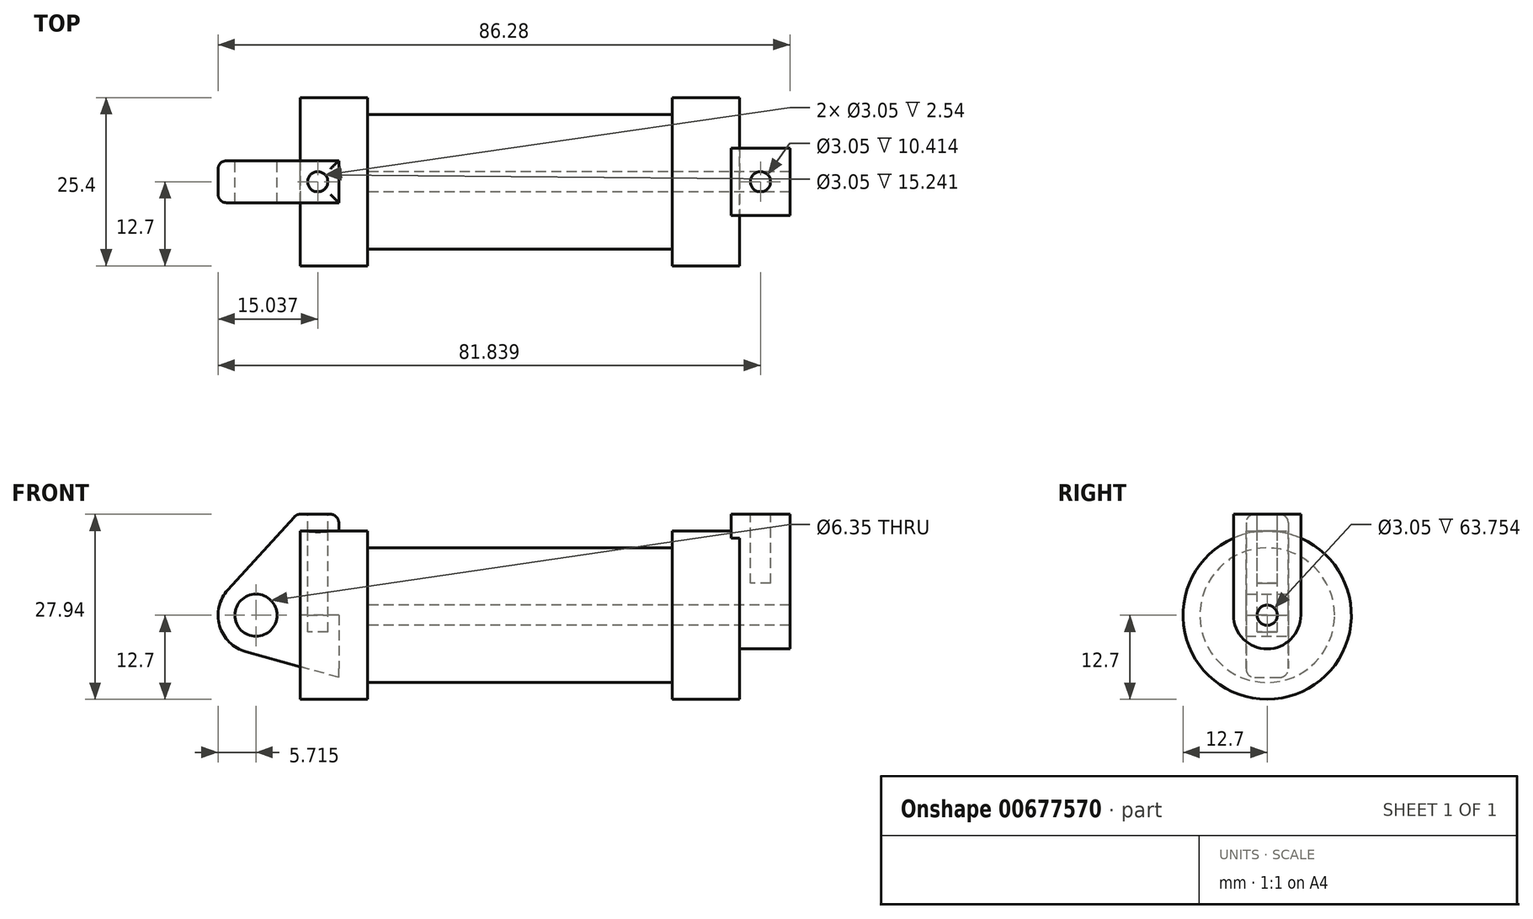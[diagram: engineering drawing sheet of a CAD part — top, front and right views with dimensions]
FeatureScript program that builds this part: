
annotation { "Feature Type Name" : "Feature", "Feature Type Description" : "" }
export const myFeature = defineFeature(function(context is Context, id is Id, definition is map)
    precondition{}
    {
        {
            var Q0;
            Q0=qCreatedBy(makeId("Front.planeOp"),FACE);
            var sketch = newSketch(context, id + "F0", { "sketchPlane" : qUnion([Q0])});
            skLineSegment(sketch, "E0", {"start": v(0, 0) * mm, "end": v(0, 12.7) * mm});
            skLineSegment(sketch, "E1", {"start": v(0, 12.7) * mm, "end": v(10.16, 12.7) * mm});
            skLineSegment(sketch, "E2", {"start": v(10.16, 12.7) * mm, "end": v(10.16, 10.16) * mm});
            skLineSegment(sketch, "E3", {"start": v(10.16, 10.16) * mm, "end": v(56.13, 10.16) * mm});
            skLineSegment(sketch, "E4", {"start": v(56.13, 10.16) * mm, "end": v(56.13, 12.7) * mm});
            skLineSegment(sketch, "E5", {"start": v(56.13, 12.7) * mm, "end": v(66.3, 12.7) * mm});
            skLineSegment(sketch, "E6", {"start": v(66.3, 12.7) * mm, "end": v(66.3, 0) * mm});
            skLineSegment(sketch, "E7", {"start": v(66.3, 0) * mm, "end": v(0, 0) * mm});
            skLineSegment(sketch, "E8", {"start": v(5.84, 15.24) * mm, "end": v(-0.5, 15.24) * mm});
            skLineSegment(sketch, "E9", {"start": v(-0.5, 15.24) * mm, "end": v(-10.88, 3.85) * mm});
            skLineSegment(sketch, "E10", {"start": v(0, 0) * mm, "end": v(-6.65, 0) * mm});
            skCircle(sketch, "E11", {"center": v(-6.65, 0) * mm, "radius": 5.72 * mm});
            skCircle(sketch, "E12", {"center": v(-6.65, 0) * mm, "radius": 3.18 * mm});
            skLineSegment(sketch, "E13", {"start": v(5.84, 15.24) * mm, "end": v(5.84, -9.4) * mm});
            skLineSegment(sketch, "E14", {"start": v(5.84, -9.4) * mm, "end": v(-8.18, -5.5) * mm});
            skSolve(sketch);
        }
        {
            var Q0;
            {var subQ0=sQuery(id+"F0.wireOp",EDGE,"E2");Q0=makeQuery(id+"F0.imprint","IMPRINT",FACE,{"disambiguationData":[TD([[makeQuery(id+"F0.imprint","IMPRINT",EDGE,{"derivedFrom":subQ0}),-1.0]])]});}
            var Q1;
            {var subQ0=sQuery(id+"F0.wireOp",EDGE,"E0");Q1=makeQuery(id+"F0.imprint","IMPRINT",FACE,{"disambiguationData":[TD([[makeQuery(id+"F0.imprint","IMPRINT",EDGE,{"derivedFrom":subQ0}),-1.0]])]});}
            var Q2;
            Q2=sQuery(id+"F0.wireOp",EDGE,"E7");
            revolve(context, id + "F1", {"entities" : qUnion([Q0, Q1]), "axis" : qUnion([Q2]), "revolveType" : RevolveType.FULL});
        }
        {
            var Q0;
            {var subQ0=sQuery(id+"F0.wireOp",EDGE,"E14");Q0=makeQuery(id+"F0.imprint","IMPRINT",FACE,{"disambiguationData":[TD([[makeQuery(id+"F0.imprint","IMPRINT",EDGE,{"derivedFrom":subQ0}),-1.0]])]});}
            var Q1;
            {var subQ1=sQuery(id+"F0.wireOp",EDGE,"E0");Q1=makeQuery(id+"F0.imprint","IMPRINT",FACE,{"disambiguationData":[TD([[makeQuery(id+"F0.imprint","IMPRINT",EDGE,{"derivedFrom":subQ1}),1.0]])]});}
            var Q2;
            {var subQ5=sQuery(id+"F0.wireOp",EDGE,"E12");Q2=makeQuery(id+"F0.imprint","IMPRINT",FACE,{"disambiguationData":[TD([[makeQuery(id+"F0.imprint","IMPRINT",EDGE,{"derivedFrom":subQ5}),-1.0]])]});}
            extrude(context, id + "F2", {"entities" : qUnion([Q0, Q1, Q2]), "endBound" : BoundingType.SYMMETRIC, "depth" : 6.35 * mm, "offsetDistance" : 25.4 * mm});
        }
        {
            var Q0;
            Q0=makeQuery(id+"F1.opRevolve","SWEPT_FACE",FACE,{"disambiguationData":[OSD([sQuery(id+"F0.wireOp",EDGE,"E6")])]});
            var sketch = newSketch(context, id + "F3", { "sketchPlane" : qUnion([Q0])});
            skCircle(sketch, "E15", {"center": v(0, 0) * mm, "radius": 1.52 * mm});
            skCircle(sketch, "E16", {"center": v(0, 0) * mm, "radius": 5.08 * mm});
            skLineSegment(sketch, "E17", {"start": v(5.08, 0) * mm, "end": v(5.08, 15.24) * mm});
            skLineSegment(sketch, "E18", {"start": v(-5.08, 0) * mm, "end": v(-5.08, 15.24) * mm});
            skLineSegment(sketch, "E19", {"start": v(-5.08, 15.24) * mm, "end": v(5.08, 15.24) * mm});
            skSolve(sketch);
        }
        {
            var Q0;
            Q0=makeQuery(id+"F3.imprint","IMPRINT",FACE,{"disambiguationData":[TD([[makeQuery(id+"F3.imprint","IMPRINT",EDGE,{"derivedFrom":sQuery(id+"F3.wireOp",EDGE,"E15")}),-1.0]])]});
            var Q1;
            {var subQ0=sQuery(id+"F3.wireOp",EDGE,"E19");Q1=makeQuery(id+"F3.imprint","IMPRINT",FACE,{"disambiguationData":[TD([[makeQuery(id+"F3.imprint","IMPRINT",EDGE,{"derivedFrom":subQ0}),-1.0]])]});}
            var Q2;
            {var subQ0=sQuery(id+"F3.wireOp",EDGE,"E17");var subQ1=sQuery(id+"F3.wireOp",EDGE,"E16");var subQ2=makeQuery(id+"F3.imprint","INTERSECT",VERTEX,{"derivedFrom":[subQ1,subQ0]});Q2=makeQuery(id+"F3.imprint","IMPRINT",FACE,{"disambiguationData":[TD([[makeQuery(id+"F3.imprint","IMPRINT",EDGE,{"disambiguationData":[TD([[subQ2,-1.0]])],"derivedFrom":subQ1}),-1.0]])]});}
            extrude(context, id + "F4", {"entities" : qUnion([Q0, Q1, Q2]), "operationType" : NewBodyOperationType.ADD, "depth" : 7.62 * mm, "offsetDistance" : 25.4 * mm, "hasSecondDirection" : true, "secondDirectionOppositeDirection" : true, "secondDirectionDepth" : 1.27 * mm});
        }
        {
            var Q0;
            Q0=makeQuery(id+"F4.boolean.opBoolean","SPLIT",FACE,{"disambiguationData":[TD([makeQuery(id+"F4.opExtrude","SWEPT_FACE",FACE,{"disambiguationData":[OSD([sQuery(id+"F3.wireOp",EDGE,"E15")])]})])],"derivedFrom":makeQuery(id+"F1.opRevolve","SWEPT_FACE",FACE,{"disambiguationData":[OSD([sQuery(id+"F0.wireOp",EDGE,"E6")])]})});
            var Q1;
            Q1=makeQuery(id+"F1.opRevolve","SWEPT_FACE",FACE,{"disambiguationData":[OSD([sQuery(id+"F0.wireOp",EDGE,"E2")])]});
            var Q2;
            Q2=makeQuery(id+"F1.opRevolve","SWEPT_BODY",BODY,{"disambiguationData":[OSD([sQuery(id+"F0.wireOp",EDGE,"E0"),sQuery(id+"F0.wireOp",EDGE,"E1"),sQuery(id+"F0.wireOp",EDGE,"E2"),sQuery(id+"F0.wireOp",EDGE,"E3"),sQuery(id+"F0.wireOp",EDGE,"E4"),sQuery(id+"F0.wireOp",EDGE,"E5"),sQuery(id+"F0.wireOp",EDGE,"E6"),sQuery(id+"F0.wireOp",EDGE,"E7")])]});
            extrude(context, id + "F5", {"entities" : qUnion([Q0]), "operationType" : NewBodyOperationType.REMOVE, "endBound" : BoundingType.UP_TO_SURFACE, "oppositeDirection" : true, "depth" : 25.4 * mm, "endBoundEntityFace" : qUnion([Q1]), "endBoundEntityBody" : qUnion([Q2]), "offsetDistance" : 25.4 * mm});
        }
        {
            var Q0;
            Q0=makeQuery(id+"F2.opExtrude","SWEPT_FACE",FACE,{"disambiguationData":[OSD([sQuery(id+"F0.wireOp",EDGE,"E8")])]});
            var sketch = newSketch(context, id + "F6", { "sketchPlane" : qUnion([Q0])});
            skCircle(sketch, "E20", {"center": v(2.67, 0) * mm, "radius": 1.52 * mm});
            skPoint(sketch, "E20.centerSnap0", {"position": v(-0.5, 0) * mm});
            skPoint(sketch, "E20.centerSnap1", {"position": v(2.67, -3.18) * mm});
            skSolve(sketch);
        }
        {
            var Q0;
            Q0=makeQuery(id+"F4.opExtrude","SWEPT_FACE",FACE,{"disambiguationData":[OSD([sQuery(id+"F3.wireOp",EDGE,"E19")])]});
            var sketch = newSketch(context, id + "F7", { "sketchPlane" : qUnion([Q0])});
            skCircle(sketch, "E21", {"center": v(69.47, 0) * mm, "radius": 1.52 * mm});
            skPoint(sketch, "E21.centerSnap0", {"position": v(69.47, -5.08) * mm});
            skPoint(sketch, "E21.centerSnap1", {"position": v(65.02, 0) * mm});
            skSolve(sketch);
        }
        {
            var Q0;
            Q0=qSketchRegion(id+"F7",true);
            extrude(context, id + "F8", {"entities" : qUnion([Q0]), "operationType" : NewBodyOperationType.REMOVE, "oppositeDirection" : true, "depth" : 10.4 * mm, "offsetDistance" : 25.4 * mm});
        }
        {
            var Q0;
            Q0=makeQuery(id+"F6.imprint","IMPRINT",FACE,{"disambiguationData":[TD([[makeQuery(id+"F6.imprint","IMPRINT",EDGE,{"derivedFrom":sQuery(id+"F6.wireOp",EDGE,"E20")}),1.0]])]});
            extrude(context, id + "F9", {"entities" : qUnion([Q0]), "operationType" : NewBodyOperationType.REMOVE, "oppositeDirection" : true, "depth" : 17.78 * mm, "offsetDistance" : 25.4 * mm});
        }
        {
            var Q0;
            Q0=makeQuery(id+"F2.opExtrude","SWEPT_EDGE",EDGE,{"disambiguationData":[OSD([sQuery(id+"F0.wireOp",EDGE,"E8"),sQuery(id+"F0.wireOp",EDGE,"E9")])]});
            var Q1;
            Q1=makeQuery(id+"F2.opExtrude","CAP_EDGE",EDGE,{"disambiguationData":[OSD([sQuery(id+"F0.wireOp",EDGE,"E8")])],"isStart":false});
            var Q2;
            Q2=makeQuery(id+"F2.opExtrude","CAP_EDGE",EDGE,{"disambiguationData":[OSD([sQuery(id+"F0.wireOp",EDGE,"E9")])],"isStart":false});
            var Q3;
            Q3=makeQuery(id+"F2.opExtrude","CAP_EDGE",EDGE,{"disambiguationData":[OSD([sQuery(id+"F0.wireOp",EDGE,"E9")])],"isStart":true});
            var Q4;
            Q4=makeQuery(id+"F2.opExtrude","CAP_EDGE",EDGE,{"disambiguationData":[OSD([sQuery(id+"F0.wireOp",EDGE,"E8")])],"isStart":true});
            var Q5;
            Q5=makeQuery(id+"F2.opExtrude","SWEPT_EDGE",EDGE,{"disambiguationData":[OSD([sQuery(id+"F0.wireOp",EDGE,"E8"),sQuery(id+"F0.wireOp",EDGE,"E13")])]});
            var Q6;
            Q6=makeQuery(id+"F1.opRevolve","SWEPT_EDGE",EDGE,{"disambiguationData":[OSD([sQuery(id+"F0.wireOp",EDGE,"E0"),sQuery(id+"F0.wireOp",EDGE,"E1")])]});
            var Q7;
            Q7=makeQuery(id+"F1.opRevolve","SWEPT_EDGE",EDGE,{"disambiguationData":[OSD([sQuery(id+"F0.wireOp",EDGE,"E1"),sQuery(id+"F0.wireOp",EDGE,"E2")])]});
            var Q8;
            Q8=makeQuery(id+"F1.opRevolve","SWEPT_EDGE",EDGE,{"disambiguationData":[OSD([sQuery(id+"F0.wireOp",EDGE,"E4"),sQuery(id+"F0.wireOp",EDGE,"E5")])]});
            var Q9;
            Q9=makeQuery(id+"F1.opRevolve","SWEPT_EDGE",EDGE,{"disambiguationData":[OSD([sQuery(id+"F0.wireOp",EDGE,"E5"),sQuery(id+"F0.wireOp",EDGE,"E6")])]});
            var Q10;
            Q10=makeQuery(id+"F4.opExtrude","SWEPT_EDGE",EDGE,{"disambiguationData":[OSD([sQuery(id+"F3.wireOp",EDGE,"E18"),sQuery(id+"F3.wireOp",EDGE,"E19")])]});
            var Q11;
            Q11=makeQuery(id+"F4.opExtrude","CAP_EDGE",EDGE,{"disambiguationData":[OSD([sQuery(id+"F3.wireOp",EDGE,"E19")])],"isStart":true});
            var Q12;
            Q12=makeQuery(id+"F4.opExtrude","SWEPT_EDGE",EDGE,{"disambiguationData":[OSD([sQuery(id+"F3.wireOp",EDGE,"E17"),sQuery(id+"F3.wireOp",EDGE,"E19")])]});
            var Q13;
            Q13=makeQuery(id+"F4.opExtrude","CAP_EDGE",EDGE,{"disambiguationData":[OSD([sQuery(id+"F3.wireOp",EDGE,"E19")])],"isStart":false});
            var Q14;
            Q14=makeQuery(id+"F1.opRevolve","SWEPT_EDGE",EDGE,{"disambiguationData":[OSD([sQuery(id+"F0.wireOp",EDGE,"E3"),sQuery(id+"F0.wireOp",EDGE,"E4")])]});
            var Q15;
            Q15=makeQuery(id+"F1.opRevolve","SWEPT_EDGE",EDGE,{"disambiguationData":[OSD([sQuery(id+"F0.wireOp",EDGE,"E2"),sQuery(id+"F0.wireOp",EDGE,"E3")])]});
            var Q16;
            Q16=makeQuery(id+"F4.boolean.opBoolean","INTERSECT",EDGE,{"derivedFrom":[makeQuery(id+"F1.opRevolve","SWEPT_FACE",FACE,{"disambiguationData":[OSD([sQuery(id+"F0.wireOp",EDGE,"E6")])]}),makeQuery(id+"F4.opExtrude","SWEPT_FACE",FACE,{"disambiguationData":[OSD([sQuery(id+"F3.wireOp",EDGE,"E17")])]})]});
            var Q17;
            Q17=makeQuery(id+"F4.opExtrude","CAP_EDGE",EDGE,{"disambiguationData":[OSD([sQuery(id+"F3.wireOp",EDGE,"E17")])],"isStart":false});
            fillet(context, id + "F10", {"entities" : qUnion([Q0, Q1, Q2, Q3, Q4, Q5, Q6, Q7, Q8, Q9, Q10, Q11, Q12, Q13, Q14, Q15, Q16, Q17]), "radius" : 1.27 * mm, "tangentPropagation" : true, "allowEdgeOverflow" : false});
        }
    });
